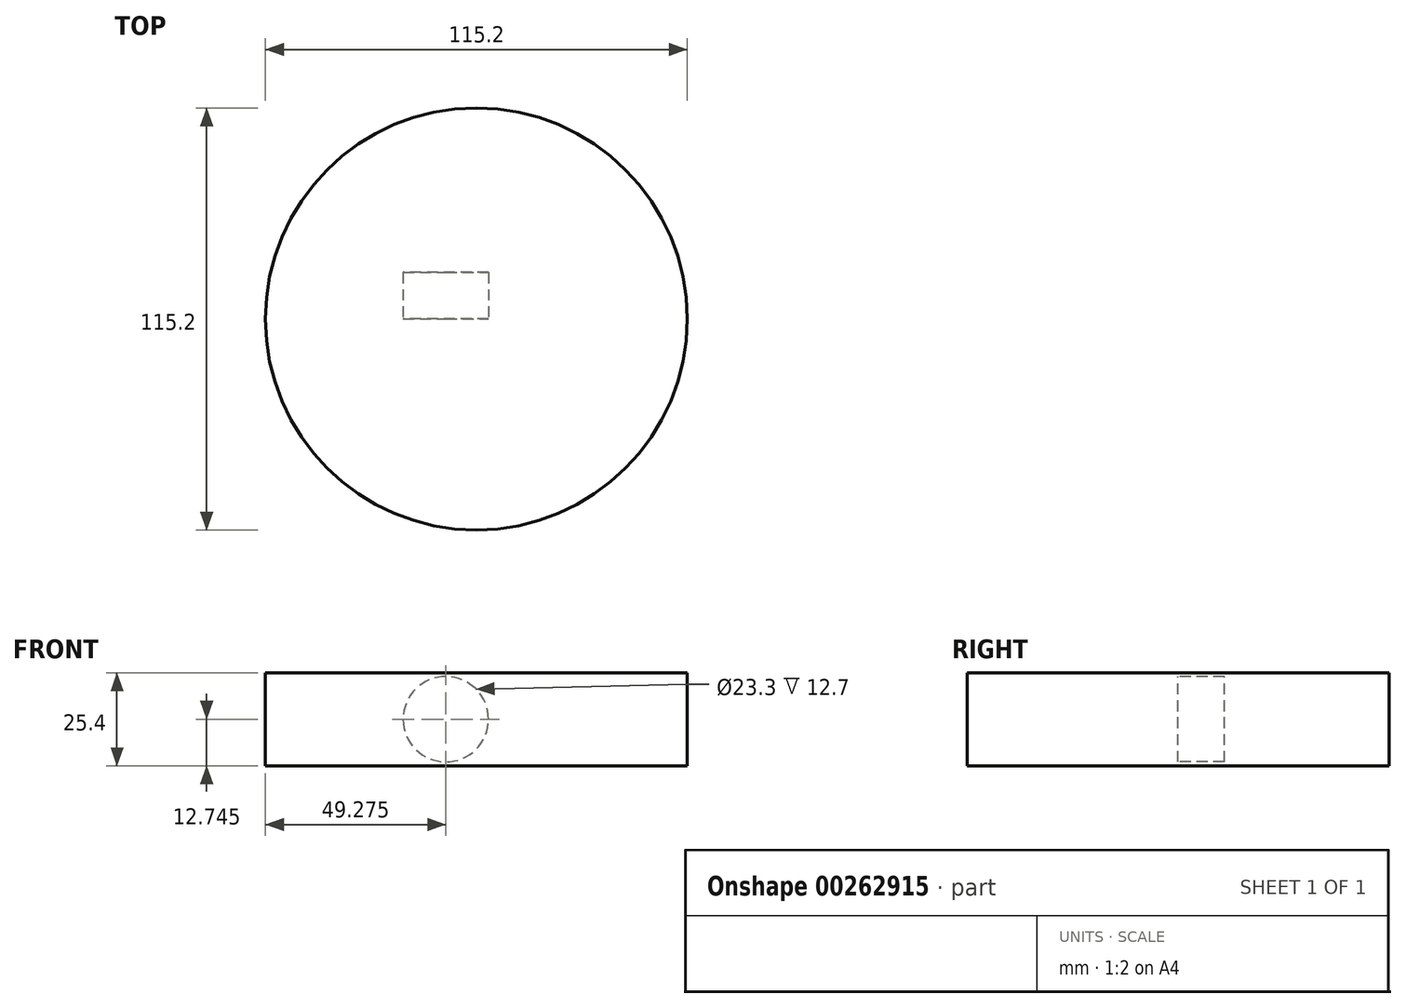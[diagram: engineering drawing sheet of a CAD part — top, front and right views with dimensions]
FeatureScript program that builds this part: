
annotation { "Feature Type Name" : "Feature", "Feature Type Description" : "" }
export const myFeature = defineFeature(function(context is Context, id is Id, definition is map)
    precondition{}
    {
        {
            var Q0;
            Q0=qCreatedBy(makeId("Top.planeOp"),FACE);
            var sketch = newSketch(context, id + "F0", { "sketchPlane" : qUnion([Q0])});
            skCircle(sketch, "E0", {"center": v(0, 0) * mm, "radius": 57.6 * mm});
            skSolve(sketch);
        }
        {
            var Q0;
            Q0 = qSketchRegion(id + "F0", true);
            extrude(context, id + "F1", {"entities" : qUnion([Q0]), "depth" : 25.4 * mm});
        }
        {
            var Q0;
            Q0=qCreatedBy(makeId("Top.planeOp"),FACE);
            var sketch = newSketch(context, id + "F2", { "sketchPlane" : qUnion([Q0])});
            skCircle(sketch, "E1", {"center": v(0, 0) * mm, "radius": 41.9 * mm});
            skSolve(sketch);
        }
        {
            var Q0;
            Q0 = qSketchRegion(id + "F2", true);
            extrude(context, id + "F3", {"entities" : qUnion([Q0]), "operationType" : NewBodyOperationType.REMOVE, "endBound" : BoundingType.THROUGH_ALL, "oppositeDirection" : true, "depth" : 25.4 * mm});
        }
        {
            var Q0;
            Q0=qCreatedBy(makeId("Front.planeOp"),FACE);
            var sketch = newSketch(context, id + "F4", { "sketchPlane" : qUnion([Q0])});
            skCircle(sketch, "E2", {"center": v(-8.32, 12.75) * mm, "radius": 11.65 * mm});
            skPoint(sketch, "E2.first.point", {"position": v(-15.82, 21.67) * mm});
            skPoint(sketch, "E2.second.point", {"position": v(0, 4.6) * mm});
            skPoint(sketch, "E2.third.point", {"position": v(-19.87, 14.27) * mm});
            skSolve(sketch);
        }
        {
            var Q0;
            Q0 = qSketchRegion(id + "F4", true);
            extrude(context, id + "F5", {"entities" : qUnion([Q0]), "operationType" : NewBodyOperationType.REMOVE, "oppositeDirection" : true, "depth" : 12.7 * mm});
        }
    });
